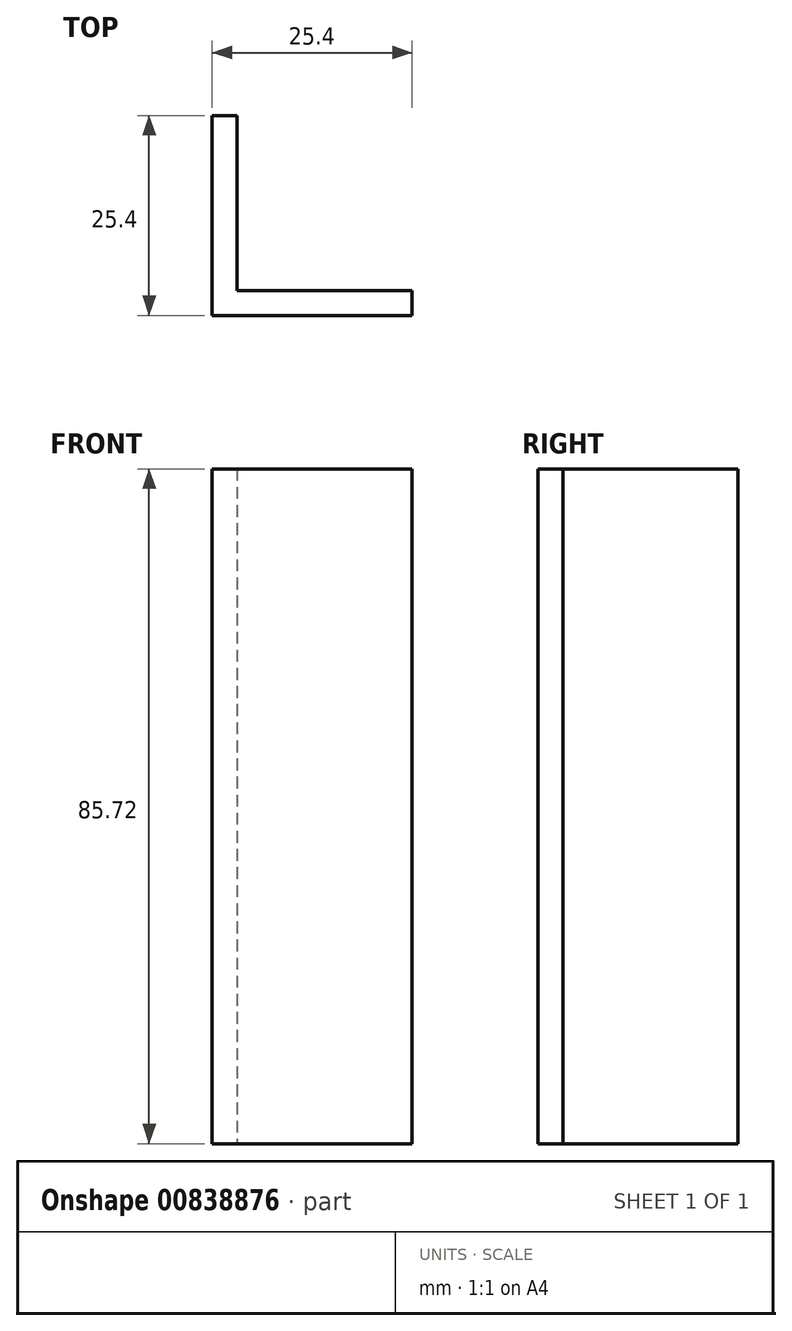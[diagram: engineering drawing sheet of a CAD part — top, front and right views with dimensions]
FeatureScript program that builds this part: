
annotation { "Feature Type Name" : "Feature", "Feature Type Description" : "" }
export const myFeature = defineFeature(function(context is Context, id is Id, definition is map)
    precondition{}
    {
        {
            var Q0;
            Q0=qCreatedBy(makeId("Top.planeOp"),FACE);
            var sketch = newSketch(context, id + "F0", { "sketchPlane" : qUnion([Q0])});
            skLineSegment(sketch, "E0", {"start": v(0, 0) * mm, "end": v(0, 25.4) * mm});
            skLineSegment(sketch, "E1", {"start": v(0, 25.4) * mm, "end": v(3.17, 25.4) * mm});
            skLineSegment(sketch, "E2", {"start": v(3.17, 25.4) * mm, "end": v(3.18, 3.17) * mm});
            skLineSegment(sketch, "E3", {"start": v(3.18, 3.17) * mm, "end": v(25.4, 3.18) * mm});
            skLineSegment(sketch, "E4", {"start": v(25.4, 3.18) * mm, "end": v(25.4, 0) * mm});
            skLineSegment(sketch, "E5", {"start": v(25.4, 0) * mm, "end": v(0, 0) * mm});
            skSolve(sketch);
        }
        {
            var Q0;
            Q0=makeQuery(id+"F0.imprint","IMPRINT",FACE,{"disambiguationData":[TD([[makeQuery(id+"F0.imprint","IMPRINT",EDGE,{"derivedFrom":sQuery(id+"F0.wireOp",EDGE,"E0")}),-1.0]])]});
            extrude(context, id + "F1", {"entities" : qUnion([Q0]), "depth" : 85.72 * mm, "offsetDistance" : 25.4 * mm});
        }
    });
